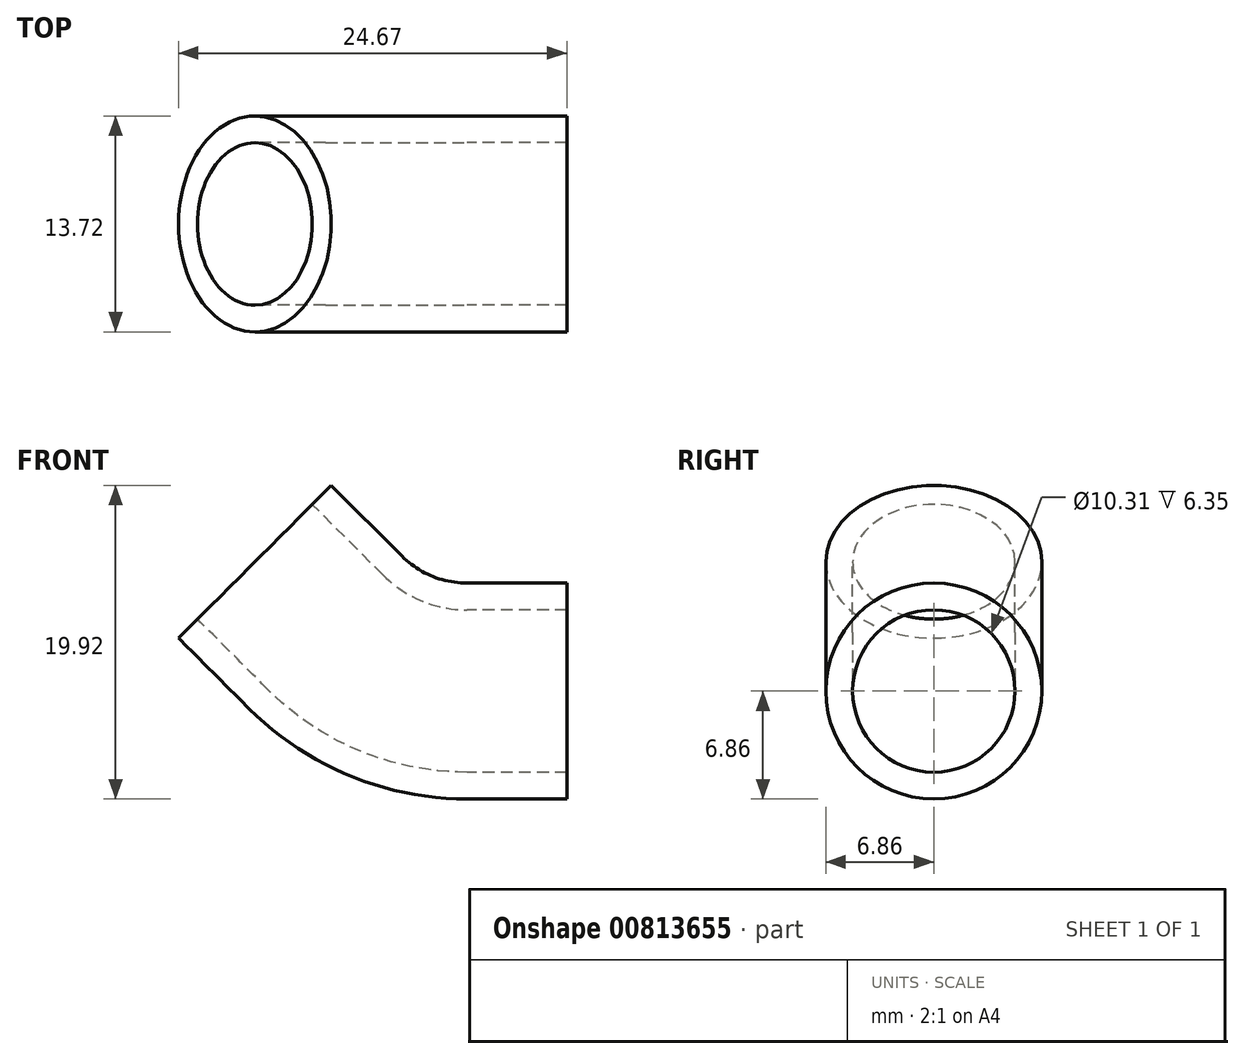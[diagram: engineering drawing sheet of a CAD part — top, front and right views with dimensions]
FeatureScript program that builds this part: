
annotation { "Feature Type Name" : "Feature", "Feature Type Description" : "" }
export const myFeature = defineFeature(function(context is Context, id is Id, definition is map)
    precondition{}
    {
        {
            var Q0;
            Q0=qCreatedBy(makeId("Front.planeOp"),FACE);
            var sketch = newSketch(context, id + "F0", { "sketchPlane" : qUnion([Q0])});
            skLineSegment(sketch, "E0", {"start": v(0, 0) * mm, "end": v(-6.35, 0) * mm});
            skLineSegment(sketch, "E1", {"start": v(-15.33, 3.72) * mm, "end": v(-19.82, 8.2) * mm});
            skPoint(sketch, "E2.visualSharp", {"position": v(-11.61, 0) * mm});
            skArc(sketch, "E2.filletArc", {"start": v(-15.33, 3.72) * mm, "mid": v(-11.21, 0.97) * mm, "end": v(-6.35, 0) * mm});
            skSolve(sketch);
        }
        {
            var Q0;
            Q0=qCreatedBy(makeId("Right.planeOp"),FACE);
            var sketch = newSketch(context, id + "F1", { "sketchPlane" : qUnion([Q0])});
            skCircle(sketch, "E3", {"center": v(0, 0) * mm, "radius": 6.86 * mm});
            skCircle(sketch, "E4", {"center": v(0, 0) * mm, "radius": 5.16 * mm});
            skSolve(sketch);
        }
        {
            var Q0;
            Q0=makeQuery(id+"F1.imprint","IMPRINT",FACE,{"disambiguationData":[TD([[makeQuery(id+"F1.imprint","IMPRINT",EDGE,{"derivedFrom":sQuery(id+"F1.wireOp",EDGE,"E3")}),1.0]])]});
            var Q1;
            Q1 = qConstructionFilter(qBodyType(qCreatedBy(id + "F0" ,EDGE), BodyType.WIRE), ConstructionObject.NO);
            sweep(context, id + "F2", {"profiles" : qUnion([Q0]), "path" : qUnion([Q1])});
        }
    });
